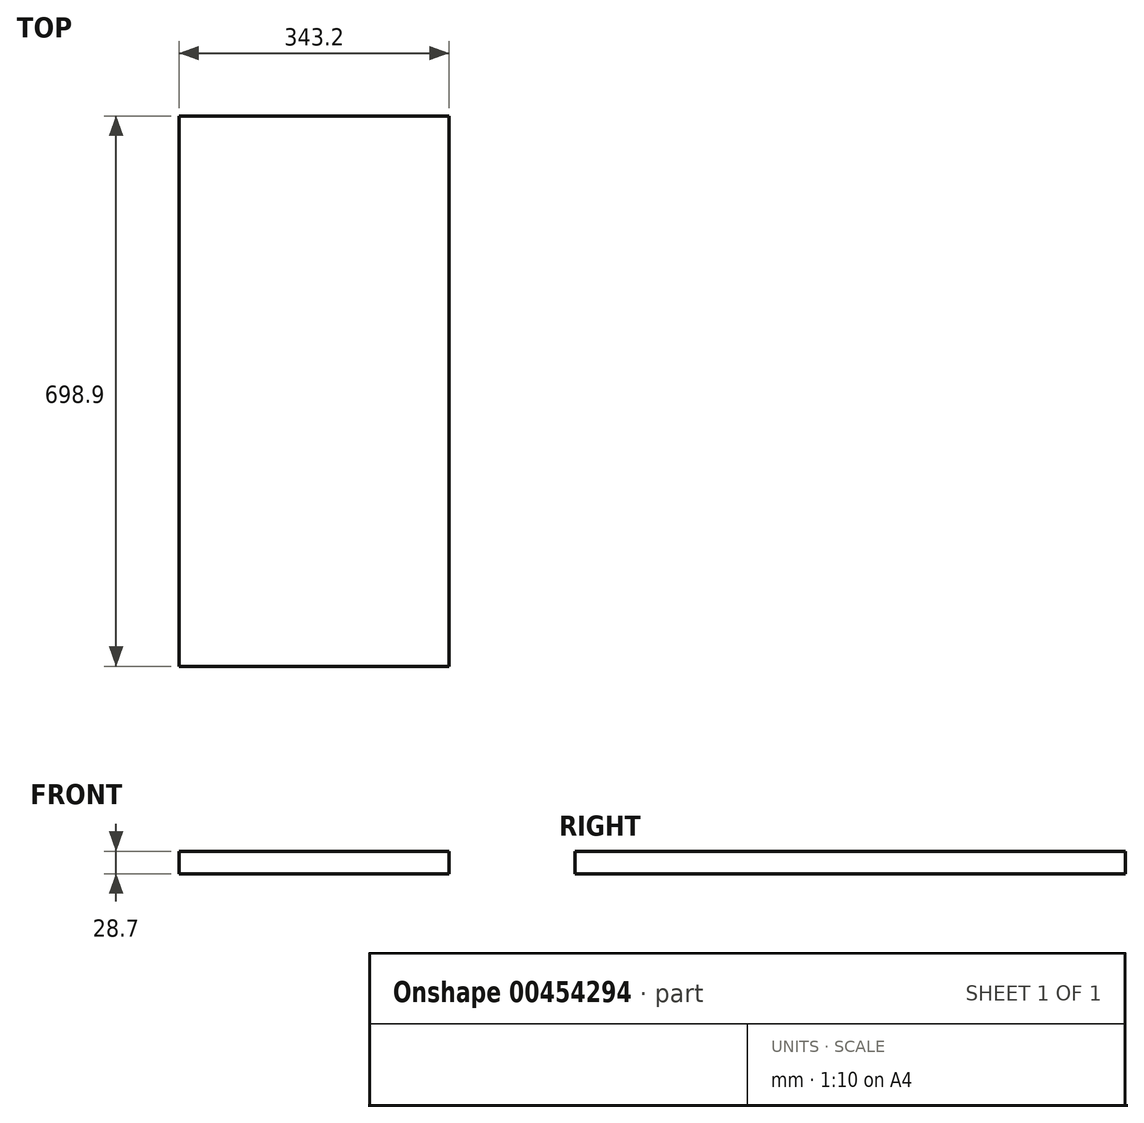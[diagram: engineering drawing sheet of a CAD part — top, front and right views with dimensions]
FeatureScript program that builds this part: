
annotation { "Feature Type Name" : "Feature", "Feature Type Description" : "" }
export const myFeature = defineFeature(function(context is Context, id is Id, definition is map)
    precondition{}
    {
        {
            var Q0;
            Q0=qCreatedBy(makeId("Top.planeOp"),FACE);
            var sketch = newSketch(context, id + "F0", { "sketchPlane" : qUnion([Q0])});
            skLineSegment(sketch, "E0.bottom", {"start": v(171.6, -349.45) * mm, "end": v(-171.6, -349.45) * mm});
            skLineSegment(sketch, "E0.top", {"start": v(171.6, 349.45) * mm, "end": v(-171.6, 349.45) * mm});
            skLineSegment(sketch, "E0.left", {"start": v(171.6, -349.45) * mm, "end": v(171.6, 349.45) * mm});
            skLineSegment(sketch, "E0.right", {"start": v(-171.6, -349.45) * mm, "end": v(-171.6, 349.45) * mm});
            skPoint(sketch, "E0.middle", {"position": v(0, 0) * mm});
            skSolve(sketch);
        }
        {
            var Q0;
            Q0=makeQuery(id+"F0.imprint","IMPRINT",FACE,{"disambiguationData":[TD([[makeQuery(id+"F0.imprint","IMPRINT",EDGE,{"derivedFrom":sQuery(id+"F0.wireOp",EDGE,"E0.bottom")}),-1.0]])]});
            extrude(context, id + "F1", {"entities" : qUnion([Q0]), "depth" : 28.7 * mm});
        }
    });
